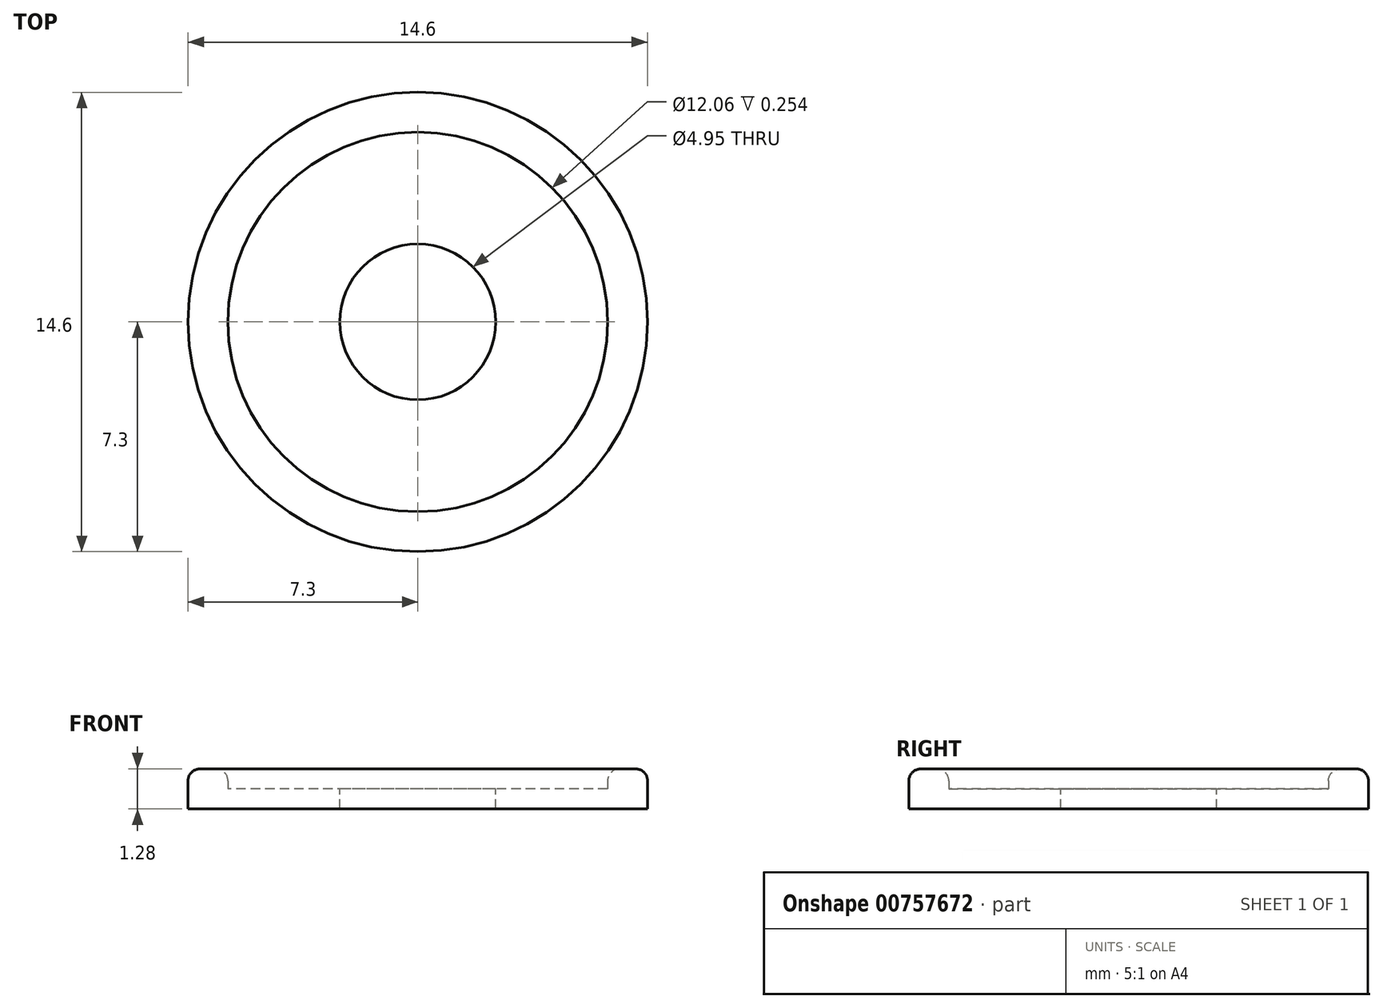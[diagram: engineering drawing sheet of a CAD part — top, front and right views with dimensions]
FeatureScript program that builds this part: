
annotation { "Feature Type Name" : "Feature", "Feature Type Description" : "" }
export const myFeature = defineFeature(function(context is Context, id is Id, definition is map)
    precondition{}
    {
        {
            var Q0;
            Q0=qCreatedBy(makeId("Top.planeOp"),FACE);
            var sketch = newSketch(context, id + "F0", { "sketchPlane" : qUnion([Q0])});
            skCircle(sketch, "E0", {"center": v(0, 0) * mm, "radius": 6.03 * mm});
            skCircle(sketch, "E1", {"center": v(0, 0) * mm, "radius": 7.3 * mm});
            skSolve(sketch);
        }
        {
            var Q0;
            Q0=makeQuery(id+"F0.imprint","IMPRINT",FACE,{"disambiguationData":[TD([[makeQuery(id+"F0.imprint","IMPRINT",EDGE,{"derivedFrom":sQuery(id+"F0.wireOp",EDGE,"E0")}),-1.0]])]});
            extrude(context, id + "F1", {"entities" : qUnion([Q0]), "depth" : 0.64 * mm, "offsetDistance" : 25.4 * mm});
        }
        {
            var Q0;
            Q0=makeQuery(id+"F1.opExtrude","CAP_FACE",FACE,{"disambiguationData":[OSD([sQuery(id+"F0.wireOp",EDGE,"E0"),sQuery(id+"F0.wireOp",EDGE,"E1")])],"isStart":false});
            fillet(context, id + "F2", {"entities" : qUnion([Q0]), "radius" : 0.38 * mm, "tangentPropagation" : true, "allowEdgeOverflow" : false});
        }
        {
            var Q0;
            Q0=qCreatedBy(makeId("Top.planeOp"),FACE);
            var sketch = newSketch(context, id + "F3", { "sketchPlane" : qUnion([Q0])});
            skCircle(sketch, "E2", {"center": v(0, 0) * mm, "radius": 7.3 * mm});
            skCircle(sketch, "E3", {"center": v(0, 0) * mm, "radius": 2.48 * mm});
            skSolve(sketch);
        }
        {
            var Q0;
            Q0=makeQuery(id+"F3.imprint","IMPRINT",FACE,{"disambiguationData":[TD([[makeQuery(id+"F3.imprint","IMPRINT",EDGE,{"derivedFrom":sQuery(id+"F3.wireOp",EDGE,"E2")}),1.0]])]});
            extrude(context, id + "F4", {"entities" : qUnion([Q0]), "operationType" : NewBodyOperationType.ADD, "oppositeDirection" : true, "depth" : 0.64 * mm, "offsetDistance" : 25.4 * mm});
        }
    });
